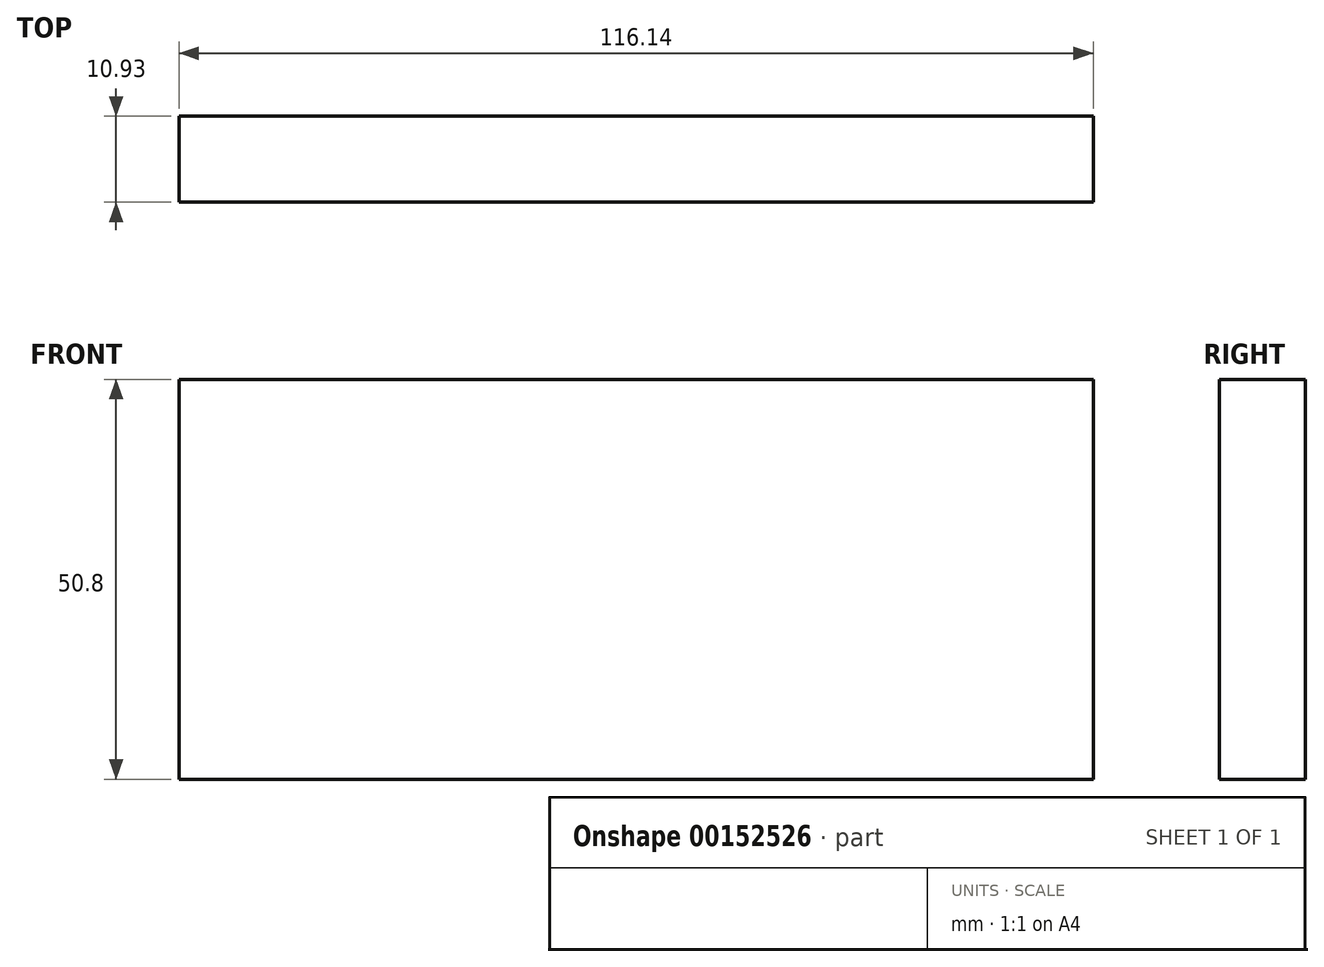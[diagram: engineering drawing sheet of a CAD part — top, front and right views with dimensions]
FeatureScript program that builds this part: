
annotation { "Feature Type Name" : "Feature", "Feature Type Description" : "" }
export const myFeature = defineFeature(function(context is Context, id is Id, definition is map)
    precondition{}
    {
        {
            var Q0;
            Q0=qCreatedBy(makeId("Top.planeOp"),FACE);
            var sketch = newSketch(context, id + "F0", { "sketchPlane" : qUnion([Q0])});
            skLineSegment(sketch, "E0.bottom", {"start": v(64.76, 65.45) * mm, "end": v(-51.38, 65.45) * mm});
            skLineSegment(sketch, "E0.top", {"start": v(64.76, 54.52) * mm, "end": v(-51.38, 54.52) * mm});
            skLineSegment(sketch, "E0.left", {"start": v(64.76, 65.45) * mm, "end": v(64.76, 54.52) * mm});
            skLineSegment(sketch, "E0.right", {"start": v(-51.38, 65.45) * mm, "end": v(-51.38, 54.52) * mm});
            skSolve(sketch);
        }
        {
            var Q0;
            Q0=makeQuery(id+"F0.imprint","IMPRINT",FACE,{"disambiguationData":[TD([[makeQuery(id+"F0.imprint","IMPRINT",EDGE,{"derivedFrom":sQuery(id+"F0.wireOp",EDGE,"E0.bottom")}),1.0]])]});
            var Q1;
            Q1=sQuery(id+"F0.wireOp",EDGE,"E0.top");
            extrude(context, id + "F1", {"entities" : qUnion([Q0]), "surfaceEntities" : qUnion([Q1]), "endBound" : BoundingType.SYMMETRIC, "depth" : 50.8 * mm});
        }
    });
